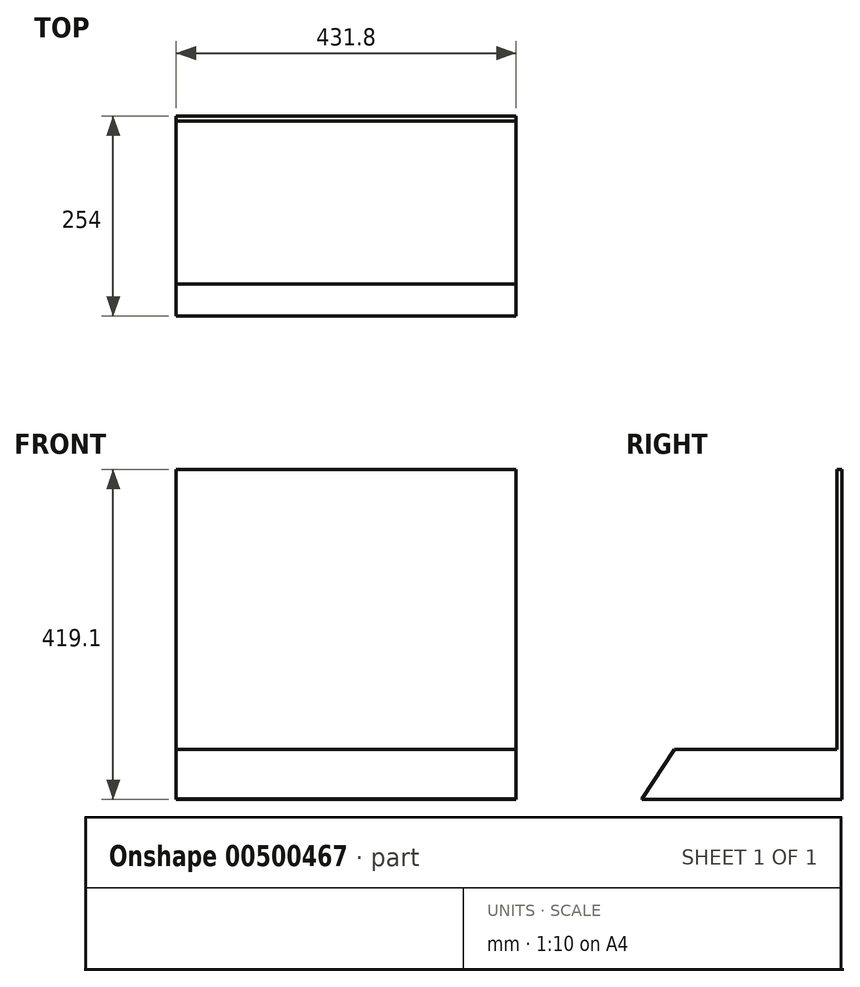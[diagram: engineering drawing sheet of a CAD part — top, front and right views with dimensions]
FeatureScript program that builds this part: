
annotation { "Feature Type Name" : "Feature", "Feature Type Description" : "" }
export const myFeature = defineFeature(function(context is Context, id is Id, definition is map)
    precondition{}
    {
        {
            var Q0;
            Q0=qCreatedBy(makeId("Front.planeOp"),FACE);
            var sketch = newSketch(context, id + "F0", { "sketchPlane" : qUnion([Q0])});
            skLineSegment(sketch, "E0.bottom", {"start": v(0, 0) * mm, "end": v(-431.8, 0) * mm});
            skLineSegment(sketch, "E0.top", {"start": v(0, 355.6) * mm, "end": v(-431.8, 355.6) * mm});
            skLineSegment(sketch, "E0.left", {"start": v(0, 0) * mm, "end": v(0, 355.6) * mm});
            skLineSegment(sketch, "E0.right", {"start": v(-431.8, 0) * mm, "end": v(-431.8, 355.6) * mm});
            skSolve(sketch);
        }
        {
            var Q0;
            Q0=makeQuery(id+"F0.imprint","IMPRINT",FACE,{"disambiguationData":[TD([[makeQuery(id+"F0.imprint","IMPRINT",EDGE,{"derivedFrom":sQuery(id+"F0.wireOp",EDGE,"E0.bottom")}),-1.0]])]});
            extrude(context, id + "F1", {"entities" : qUnion([Q0]), "depth" : 6.35 * mm});
        }
        {
            var Q0;
            Q0=qCreatedBy(makeId("Front.planeOp"),FACE);
            var sketch = newSketch(context, id + "F2", { "sketchPlane" : qUnion([Q0])});
            skLineSegment(sketch, "E1.bottom", {"start": v(0, 0) * mm, "end": v(-431.8, 0) * mm});
            skLineSegment(sketch, "E1.top", {"start": v(0, -63.5) * mm, "end": v(-431.8, -63.5) * mm});
            skLineSegment(sketch, "E1.left", {"start": v(0, 0) * mm, "end": v(0, -63.5) * mm});
            skLineSegment(sketch, "E1.right", {"start": v(-431.8, 0) * mm, "end": v(-431.8, -63.5) * mm});
            skSolve(sketch);
        }
        {
            var Q0;
            Q0=makeQuery(id+"F2.imprint","IMPRINT",FACE,{"disambiguationData":[TD([[makeQuery(id+"F2.imprint","IMPRINT",EDGE,{"derivedFrom":sQuery(id+"F2.wireOp",EDGE,"E1.bottom")}),1.0]])]});
            extrude(context, id + "F3", {"entities" : qUnion([Q0]), "operationType" : NewBodyOperationType.ADD, "depth" : 254 * mm});
        }
        {
            var Q0;
            Q0=qCreatedBy(makeId("Right.planeOp"),FACE);
            var sketch = newSketch(context, id + "F4", { "sketchPlane" : qUnion([Q0])});
            skLineSegment(sketch, "E2", {"start": v(-255.74, -65.32) * mm, "end": v(-172.8, 61.94) * mm});
            skLineSegment(sketch, "E3", {"start": v(-172.8, 61.94) * mm, "end": v(-330.2, 41.2) * mm});
            skLineSegment(sketch, "E4", {"start": v(-330.2, 41.2) * mm, "end": v(-255.74, -65.32) * mm});
            skSolve(sketch);
        }
        {
            var Q0;
            Q0 = qSketchRegion(id + "F4", true);
            extrude(context, id + "F5", {"entities" : qUnion([Q0]), "operationType" : NewBodyOperationType.REMOVE, "endBound" : BoundingType.THROUGH_ALL, "oppositeDirection" : true, "depth" : 25.4 * mm});
        }
    });
